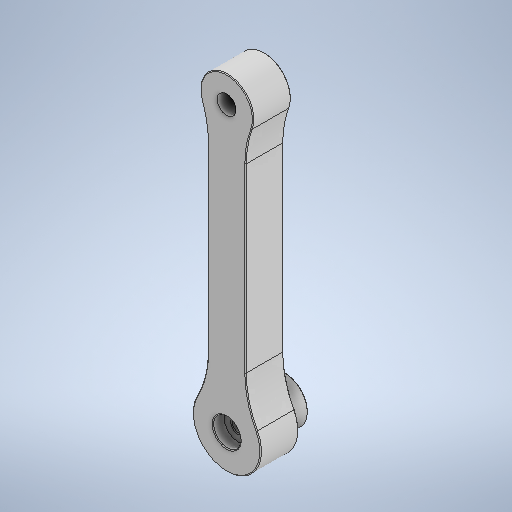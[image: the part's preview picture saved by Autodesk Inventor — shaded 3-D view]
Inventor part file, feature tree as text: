
AUTODESK INVENTOR PART (.ipt)
format: ipt  version: 2025.1 (Build 291241000, 241)  size: 345,600 bytes
history: native  units: mm
features: extrude x5, sketch x4, fillet x4
ambient origin geometry x8: Origin, YZ Plane, XZ Plane, XY Plane, X Axis, Y Axis, Z Axis, Center Point
bodies: Volumenkörper1 (feature_tree)
feature tree (13):
  sketch  "Skizze1"  dims[d2=18.0mm d4=25.0mm]
  extrude  "Extrusion1"  Depth=25.0mm
  extrude  "Extrusion5"  TaperAngle=0.0deg  [1 undecoded]
  fillet  "Rundung3"  Radius=5.0mm
  fillet  "Rundung4"  Radius=5.0mm
  extrude  "Extrusion6"  Depth=5.5mm TaperAngle=0.0deg
  extrude  "Extrusion7"  Depth=0.2mm
  fillet  "Rundung5"  Radius=7.3mm
  fillet  "Rundung6"  Radius=3.0mm
  extrude  "Extrusion8"  Depth=9.0mm
  sketch  "Skizze8"  dims[d6=10.0mm d7=0.0mm d10=0.0mm d33=5.0mm d34=5.0mm]
  sketch  "Skizze10"  dims[d36=12.0mm d37=5.5mm d38=0.0mm]
  sketch  "Skizze11"  dims[d39=0.2mm d40=0.2mm d41=7.3mm d42=3.0mm d43=0.0mm d44=3.5mm d45=3.0mm d46=0.0mm d47=0.2mm d48=0.2mm d49=75.0mm d51=5.0mm d52=9.0mm d53=0.0mm d54=14.0mm]
note: 1 required parameter value undecoded (feature->parameter linkage not recoverable at this tier; creation-order binding heuristic only, values carry confidence <= 0.55)
